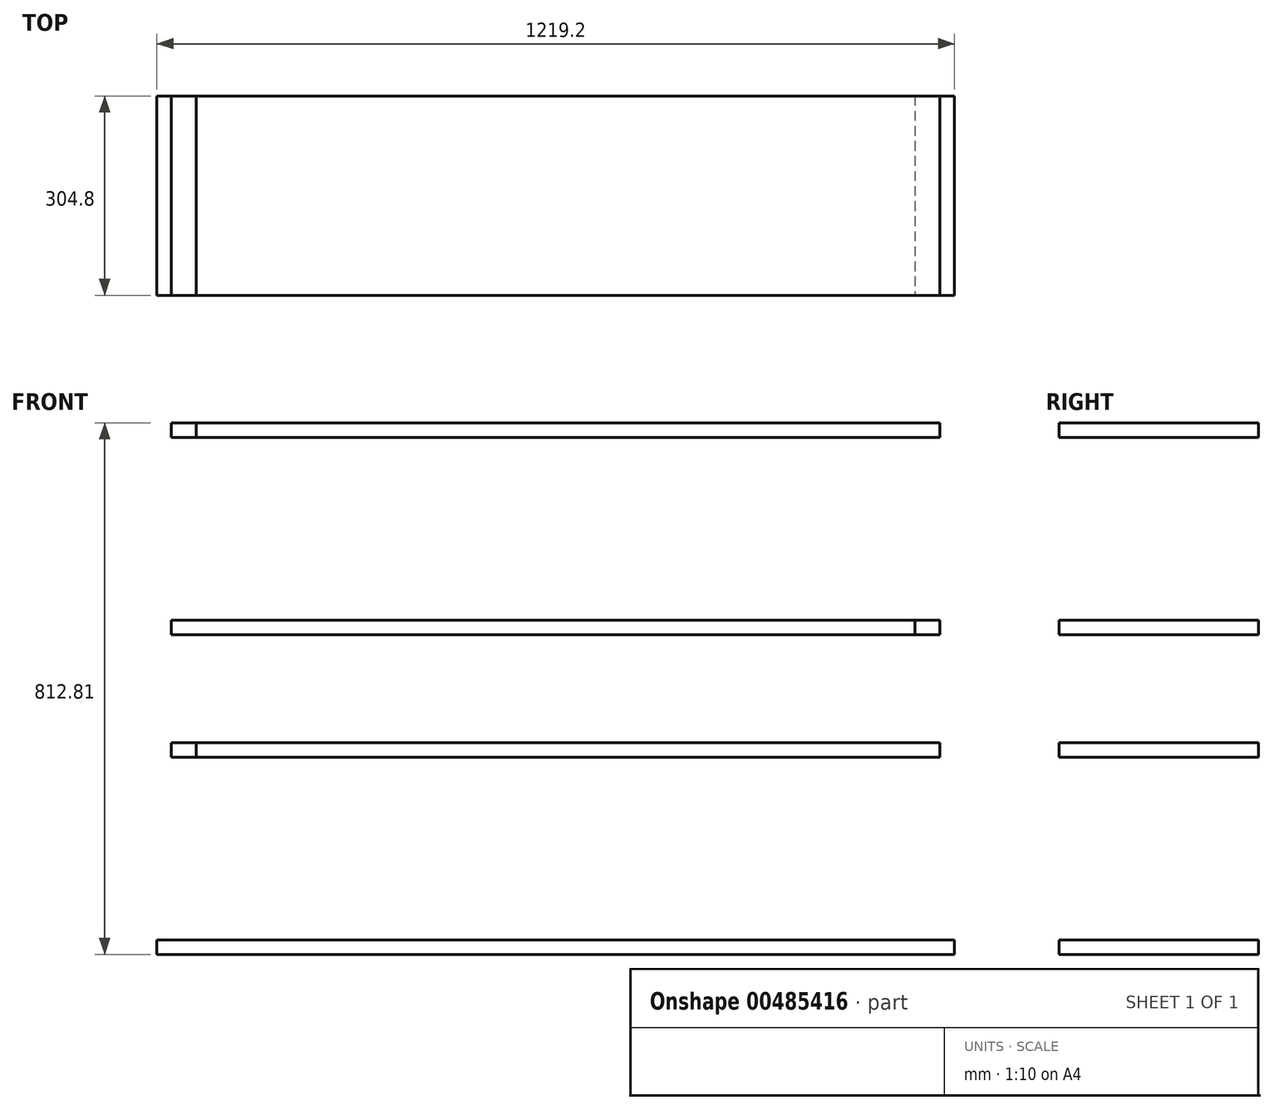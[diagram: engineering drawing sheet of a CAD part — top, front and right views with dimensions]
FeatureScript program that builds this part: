
annotation { "Feature Type Name" : "Feature", "Feature Type Description" : "" }
export const myFeature = defineFeature(function(context is Context, id is Id, definition is map)
    precondition{}
    {
        {
            var Q0;
            Q0=qCreatedBy(makeId("Front.planeOp"),FACE);
            var sketch = newSketch(context, id + "F0", { "sketchPlane" : qUnion([Q0])});
            skLineSegment(sketch, "E0.bottom", {"start": v(0, 0) * mm, "end": v(-1219.2, 0) * mm});
            skLineSegment(sketch, "E0.top", {"start": v(0, -22.23) * mm, "end": v(-1219.2, -22.23) * mm});
            skLineSegment(sketch, "E0.left", {"start": v(0, 0) * mm, "end": v(0, -22.23) * mm});
            skLineSegment(sketch, "E0.right", {"start": v(-1219.2, 0) * mm, "end": v(-1219.2, -22.23) * mm});
            skLineSegment(sketch, "E1.bottom", {"start": v(0, 0) * mm, "end": v(-22.22, 0) * mm});
            skLineSegment(sketch, "E1.top", {"start": v(0, 790.58) * mm, "end": v(-22.23, 790.58) * mm});
            skLineSegment(sketch, "E1.left", {"start": v(0, 0) * mm, "end": v(0, 790.58) * mm});
            skLineSegment(sketch, "E1.right", {"start": v(-22.22, 0) * mm, "end": v(-22.23, 790.58) * mm});
            skLineSegment(sketch, "E2.bottom", {"start": v(-1219.2, 0) * mm, "end": v(-1196.98, 0) * mm});
            skLineSegment(sketch, "E2.top", {"start": v(-1219.2, 790.57) * mm, "end": v(-1196.98, 790.57) * mm});
            skLineSegment(sketch, "E2.left", {"start": v(-1219.2, 0) * mm, "end": v(-1219.2, 790.57) * mm});
            skLineSegment(sketch, "E2.right", {"start": v(-1196.98, 0) * mm, "end": v(-1196.98, 790.57) * mm});
            skLineSegment(sketch, "E3.bottom", {"start": v(-22.22, 301.63) * mm, "end": v(-1158.88, 301.62) * mm});
            skLineSegment(sketch, "E3.top", {"start": v(-22.22, 279.4) * mm, "end": v(-1158.88, 279.4) * mm});
            skLineSegment(sketch, "E3.left", {"start": v(-22.22, 301.63) * mm, "end": v(-22.22, 279.4) * mm});
            skLineSegment(sketch, "E3.right", {"start": v(-1158.88, 301.63) * mm, "end": v(-1158.88, 279.4) * mm});
            skLineSegment(sketch, "E4.bottom", {"start": v(-1196.98, 466.72) * mm, "end": v(-60.32, 466.72) * mm});
            skLineSegment(sketch, "E4.top", {"start": v(-1196.98, 488.95) * mm, "end": v(-60.32, 488.95) * mm});
            skLineSegment(sketch, "E4.left", {"start": v(-1196.98, 466.72) * mm, "end": v(-1196.98, 488.95) * mm});
            skLineSegment(sketch, "E4.right", {"start": v(-60.32, 466.72) * mm, "end": v(-60.32, 488.95) * mm});
            skLineSegment(sketch, "E5.bottom", {"start": v(-22.23, 790.58) * mm, "end": v(-1158.88, 790.57) * mm});
            skLineSegment(sketch, "E5.top", {"start": v(-22.23, 768.35) * mm, "end": v(-1158.88, 768.35) * mm});
            skLineSegment(sketch, "E5.left", {"start": v(-22.23, 790.58) * mm, "end": v(-22.23, 768.35) * mm});
            skLineSegment(sketch, "E5.right", {"start": v(-1158.88, 790.57) * mm, "end": v(-1158.88, 768.35) * mm});
            skLineSegment(sketch, "E6.bottom", {"start": v(-1158.88, 301.62) * mm, "end": v(-1196.98, 301.62) * mm});
            skLineSegment(sketch, "E6.top", {"start": v(-1158.88, 279.4) * mm, "end": v(-1196.98, 279.4) * mm});
            skLineSegment(sketch, "E6.left", {"start": v(-1158.88, 301.62) * mm, "end": v(-1158.88, 279.4) * mm});
            skLineSegment(sketch, "E6.right", {"start": v(-1196.98, 301.62) * mm, "end": v(-1196.98, 279.4) * mm});
            skLineSegment(sketch, "E7.bottom", {"start": v(-60.32, 488.95) * mm, "end": v(-22.22, 488.95) * mm});
            skLineSegment(sketch, "E7.top", {"start": v(-60.32, 466.72) * mm, "end": v(-22.22, 466.72) * mm});
            skLineSegment(sketch, "E7.left", {"start": v(-60.32, 488.95) * mm, "end": v(-60.32, 466.72) * mm});
            skLineSegment(sketch, "E7.right", {"start": v(-22.22, 488.95) * mm, "end": v(-22.22, 466.72) * mm});
            skLineSegment(sketch, "E8.bottom", {"start": v(-1158.88, 790.57) * mm, "end": v(-1196.98, 790.57) * mm});
            skLineSegment(sketch, "E8.top", {"start": v(-1158.88, 768.35) * mm, "end": v(-1196.98, 768.35) * mm});
            skLineSegment(sketch, "E8.right", {"start": v(-1196.98, 790.57) * mm, "end": v(-1196.98, 768.35) * mm});
            skSolve(sketch);
        }
        {
            var Q0;
            Q0=makeQuery(id+"F0.imprint","IMPRINT",FACE,{"disambiguationData":[TD([[makeQuery(id+"F0.imprint","IMPRINT",EDGE,{"derivedFrom":sQuery(id+"F0.wireOp",EDGE,"E5.bottom")}),1.0]])]});
            var Q1;
            {var subQ1=sQuery(id+"F0.wireOp",EDGE,"E2.bottom");Q1=makeQuery(id+"F0.imprint","IMPRINT",FACE,{"disambiguationData":[TD([[makeQuery(id+"F0.imprint","IMPRINT",EDGE,{"derivedFrom":subQ1}),1.0]])]});}
            var Q2;
            Q2=makeQuery(id+"F0.imprint","IMPRINT",FACE,{"disambiguationData":[TD([[makeQuery(id+"F0.imprint","IMPRINT",EDGE,{"derivedFrom":sQuery(id+"F0.wireOp",EDGE,"E4.bottom")}),1.0]])]});
            var Q3;
            {var subQ1=sQuery(id+"F0.wireOp",EDGE,"E1.bottom");Q3=makeQuery(id+"F0.imprint","IMPRINT",FACE,{"disambiguationData":[TD([[makeQuery(id+"F0.imprint","IMPRINT",EDGE,{"derivedFrom":subQ1}),-1.0]])]});}
            var Q4;
            Q4=makeQuery(id+"F0.imprint","IMPRINT",FACE,{"disambiguationData":[TD([[makeQuery(id+"F0.imprint","IMPRINT",EDGE,{"derivedFrom":sQuery(id+"F0.wireOp",EDGE,"E3.bottom")}),1.0]])]});
            var Q5;
            Q5=makeQuery(id+"F0.imprint","IMPRINT",FACE,{"disambiguationData":[TD([[makeQuery(id+"F0.imprint","IMPRINT",EDGE,{"derivedFrom":sQuery(id+"F0.wireOp",EDGE,"E0.bottom")}),1.0]])]});
            extrude(context, id + "F1", {"entities" : qUnion([Q0, Q1, Q2, Q3, Q4, Q5]), "oppositeDirection" : true, "depth" : 304.8 * mm});
        }
        {
            var Q0;
            Q0=makeQuery(id+"F0.imprint","IMPRINT",FACE,{"disambiguationData":[TD([[makeQuery(id+"F0.imprint","IMPRINT",EDGE,{"derivedFrom":sQuery(id+"F0.wireOp",EDGE,"E8.bottom")}),1.0]])]});
            var Q1;
            Q1=makeQuery(id+"F0.imprint","IMPRINT",FACE,{"disambiguationData":[TD([[makeQuery(id+"F0.imprint","IMPRINT",EDGE,{"derivedFrom":sQuery(id+"F0.wireOp",EDGE,"E7.bottom")}),-1.0]])]});
            var Q2;
            Q2=makeQuery(id+"F0.imprint","IMPRINT",FACE,{"disambiguationData":[TD([[makeQuery(id+"F0.imprint","IMPRINT",EDGE,{"derivedFrom":sQuery(id+"F0.wireOp",EDGE,"E6.bottom")}),1.0]])]});
            extrude(context, id + "F2", {"entities" : qUnion([Q0, Q1, Q2]), "oppositeDirection" : true, "depth" : 304.8 * mm});
        }
    });
